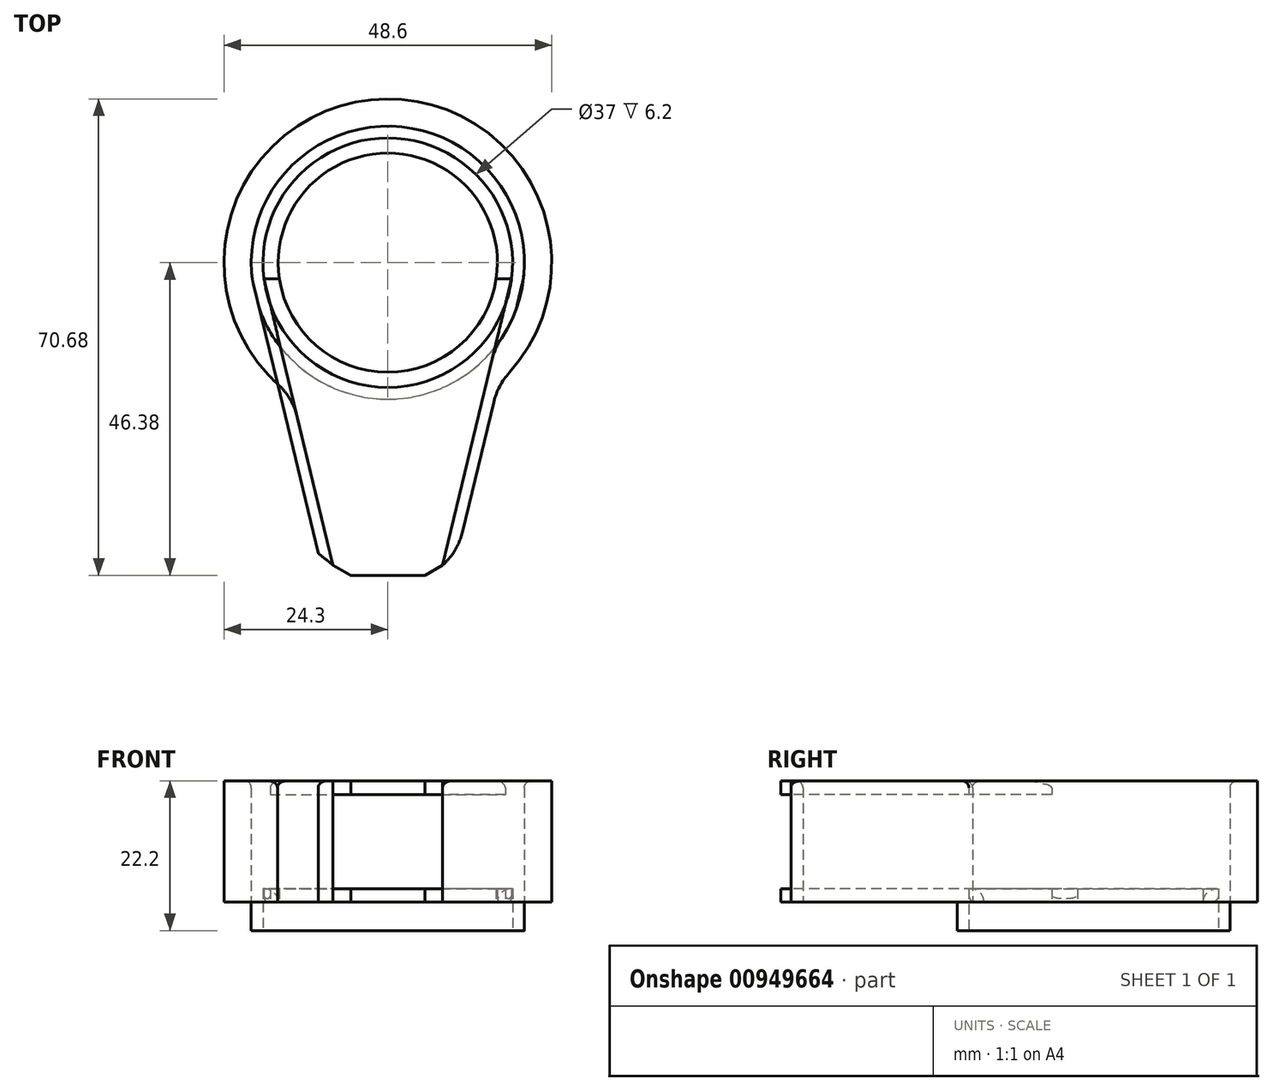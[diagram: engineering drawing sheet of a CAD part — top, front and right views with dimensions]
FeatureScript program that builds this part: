
annotation { "Feature Type Name" : "Feature", "Feature Type Description" : "" }
export const myFeature = defineFeature(function(context is Context, id is Id, definition is map)
    precondition{}
    {
        {
            var Q0;
            Q0=qCreatedBy(makeId("Top.planeOp"),FACE);
            var sketch = newSketch(context, id + "F0", { "sketchPlane" : qUnion([Q0])});
            skCircle(sketch, "E0", {"center": v(0, 0) * mm, "radius": 20.25 * mm});
            skCircle(sketch, "E1", {"center": v(0, 0) * mm, "radius": 24.3 * mm});
            skCircle(sketch, "E2", {"center": v(0, 0) * mm, "radius": 18.5 * mm});
            skArc(sketch, "E3", {"start": v(16.07, -2.4) * mm, "mid": v(0, 16.25) * mm, "end": v(-16.07, -2.4) * mm});
            skLineSegment(sketch, "E4", {"start": v(0, 0) * mm, "end": v(0, -46.38) * mm, "construction": true});
            skLineSegment(sketch, "E5", {"start": v(-16.07, -2.4) * mm, "end": v(-5.5, -46.38) * mm});
            skLineSegment(sketch, "E6", {"start": v(-5.5, -46.38) * mm, "end": v(0, -46.38) * mm});
            skLineSegment(sketch, "E7", {"start": v(-18.34, -2.4) * mm, "end": v(-8.13, -44.88) * mm});
            skLineSegment(sketch, "E8", {"start": v(-8.13, -44.88) * mm, "end": v(-5.5, -46.38) * mm});
            skLineSegment(sketch, "E9.MirrorCS", {"start": v(16.07, -2.4) * mm, "end": v(5.5, -46.38) * mm});
            skLineSegment(sketch, "E10.MirrorCS", {"start": v(18.34, -2.4) * mm, "end": v(8.13, -44.88) * mm});
            skLineSegment(sketch, "E11.MirrorCS", {"start": v(8.13, -44.88) * mm, "end": v(5.5, -46.38) * mm});
            skLineSegment(sketch, "E12.MirrorCS", {"start": v(5.5, -46.38) * mm, "end": v(0, -46.38) * mm});
            skLineSegment(sketch, "E13", {"start": v(-16.07, -2.4) * mm, "end": v(16.07, -2.4) * mm, "construction": true});
            skLineSegment(sketch, "E14", {"start": v(16.07, -2.4) * mm, "end": v(-16.07, -2.4) * mm});
            skLineSegment(sketch, "E15", {"start": v(-20.1, -2.4) * mm, "end": v(-10.32, -43.1) * mm});
            skLineSegment(sketch, "E16", {"start": v(-10.32, -43.1) * mm, "end": v(-8.13, -44.88) * mm});
            skLineSegment(sketch, "E17.MirrorCS", {"start": v(20.1, -2.4) * mm, "end": v(10.32, -43.1) * mm});
            skLineSegment(sketch, "E18.MirrorCS", {"start": v(10.32, -43.1) * mm, "end": v(8.13, -44.88) * mm});
            skCircle(sketch, "E19", {"center": v(0, 0) * mm, "radius": 16.25 * mm});
            skLineSegment(sketch, "E20", {"start": v(-16.07, -2.4) * mm, "end": v(-18.34, -2.4) * mm});
            skLineSegment(sketch, "E21", {"start": v(16.07, -2.4) * mm, "end": v(18.34, -2.4) * mm});
            skSolve(sketch);
        }
        {
            var Q0;
            {var subQ0=sQuery(id+"F0.wireOp",EDGE,"E3");Q0=makeQuery(id+"F0.imprint","IMPRINT",FACE,{"disambiguationData":[TD([[makeQuery(id+"F0.imprint","IMPRINT",EDGE,{"derivedFrom":subQ0}),-1.0]])]});}
            var Q1;
            {var subQ5=sQuery(id+"F0.wireOp",EDGE,"E8");Q1=makeQuery(id+"F0.imprint","IMPRINT",FACE,{"disambiguationData":[TD([[makeQuery(id+"F0.imprint","IMPRINT",EDGE,{"derivedFrom":subQ5}),1.0]])]});}
            var Q2;
            {var subQ5=sQuery(id+"F0.wireOp",EDGE,"E11.MirrorCS");Q2=makeQuery(id+"F0.imprint","IMPRINT",FACE,{"disambiguationData":[TD([[makeQuery(id+"F0.imprint","IMPRINT",EDGE,{"derivedFrom":subQ5}),-1.0]])]});}
            var Q3;
            {var subQ0=sQuery(id+"F0.wireOp",EDGE,"E9.MirrorCS");var subQ1=sQuery(id+"F0.wireOp",EDGE,"E0");var subQ2=makeQuery(id+"F0.imprint","INTERSECT",VERTEX,{"derivedFrom":[subQ1,subQ0]});Q3=makeQuery(id+"F0.imprint","IMPRINT",FACE,{"disambiguationData":[TD([[makeQuery(id+"F0.imprint","IMPRINT",EDGE,{"disambiguationData":[TD([[subQ2,-1.0]])],"derivedFrom":subQ1}),-1.0]])]});}
            var Q4;
            {var subQ0=sQuery(id+"F0.wireOp",EDGE,"E5");var subQ1=sQuery(id+"F0.wireOp",EDGE,"E0");var subQ2=makeQuery(id+"F0.imprint","INTERSECT",VERTEX,{"derivedFrom":[subQ1,subQ0]});Q4=makeQuery(id+"F0.imprint","IMPRINT",FACE,{"disambiguationData":[TD([[makeQuery(id+"F0.imprint","IMPRINT",EDGE,{"disambiguationData":[TD([[subQ2,1.0]])],"derivedFrom":subQ1}),-1.0]])]});}
            var Q5;
            {var subQ0=sQuery(id+"F0.wireOp",EDGE,"E9.MirrorCS");var subQ1=sQuery(id+"F0.wireOp",EDGE,"E0");var subQ2=makeQuery(id+"F0.imprint","INTERSECT",VERTEX,{"derivedFrom":[subQ1,subQ0]});Q5=makeQuery(id+"F0.imprint","IMPRINT",FACE,{"disambiguationData":[TD([[makeQuery(id+"F0.imprint","IMPRINT",EDGE,{"disambiguationData":[TD([[subQ2,-1.0]])],"derivedFrom":subQ1}),1.0]])]});}
            var Q6;
            {var subQ0=sQuery(id+"F0.wireOp",EDGE,"E5");var subQ1=sQuery(id+"F0.wireOp",EDGE,"E0");var subQ2=makeQuery(id+"F0.imprint","INTERSECT",VERTEX,{"derivedFrom":[subQ1,subQ0]});Q6=makeQuery(id+"F0.imprint","IMPRINT",FACE,{"disambiguationData":[TD([[makeQuery(id+"F0.imprint","IMPRINT",EDGE,{"disambiguationData":[TD([[subQ2,1.0]])],"derivedFrom":subQ1}),1.0]])]});}
            var Q7;
            {var subQ0=sQuery(id+"F0.wireOp",EDGE,"E6");Q7=makeQuery(id+"F0.imprint","IMPRINT",FACE,{"disambiguationData":[TD([[makeQuery(id+"F0.imprint","IMPRINT",EDGE,{"derivedFrom":subQ0}),1.0]])]});}
            var Q8;
            {var subQ0=sQuery(id+"F0.wireOp",EDGE,"E5");var subQ1=sQuery(id+"F0.wireOp",EDGE,"E0");var subQ2=makeQuery(id+"F0.imprint","INTERSECT",VERTEX,{"derivedFrom":[subQ1,subQ0]});Q8=makeQuery(id+"F0.imprint","IMPRINT",FACE,{"disambiguationData":[TD([[makeQuery(id+"F0.imprint","IMPRINT",EDGE,{"disambiguationData":[TD([[subQ2,-1.0]])],"derivedFrom":subQ1}),-1.0]])]});}
            var Q9;
            {var subQ0=sQuery(id+"F0.wireOp",EDGE,"E5");var subQ1=sQuery(id+"F0.wireOp",EDGE,"E0");var subQ2=makeQuery(id+"F0.imprint","INTERSECT",VERTEX,{"derivedFrom":[subQ1,subQ0]});Q9=makeQuery(id+"F0.imprint","IMPRINT",FACE,{"disambiguationData":[TD([[makeQuery(id+"F0.imprint","IMPRINT",EDGE,{"disambiguationData":[TD([[subQ2,-1.0]])],"derivedFrom":subQ1}),1.0]])]});}
            extrude(context, id + "F1", {"entities" : qUnion([Q0, Q1, Q2, Q3, Q4, Q5, Q6, Q7, Q8, Q9]), "depth" : 2 * mm, "offsetDistance" : 25 * mm});
        }
        {
            var Q0;
            {var subQ0=sQuery(id+"F0.wireOp",EDGE,"E7");var subQ1=sQuery(id+"F0.wireOp",EDGE,"E0");var subQ2=makeQuery(id+"F0.imprint","INTERSECT",VERTEX,{"derivedFrom":[subQ1,subQ0]});Q0=makeQuery(id+"F0.imprint","IMPRINT",FACE,{"disambiguationData":[TD([[makeQuery(id+"F0.imprint","IMPRINT",EDGE,{"disambiguationData":[TD([[subQ2,1.0]])],"derivedFrom":subQ1}),1.0]])]});}
            var Q1;
            {var subQ0=sQuery(id+"F0.wireOp",EDGE,"E5");var subQ1=sQuery(id+"F0.wireOp",EDGE,"E0");var subQ2=makeQuery(id+"F0.imprint","INTERSECT",VERTEX,{"derivedFrom":[subQ1,subQ0]});Q1=makeQuery(id+"F0.imprint","IMPRINT",FACE,{"disambiguationData":[TD([[makeQuery(id+"F0.imprint","IMPRINT",EDGE,{"disambiguationData":[TD([[subQ2,-1.0]])],"derivedFrom":subQ1}),1.0]])]});}
            var Q2;
            {var subQ0=sQuery(id+"F0.wireOp",EDGE,"E7");var subQ1=sQuery(id+"F0.wireOp",EDGE,"E0");var subQ2=makeQuery(id+"F0.imprint","INTERSECT",VERTEX,{"derivedFrom":[subQ1,subQ0]});Q2=makeQuery(id+"F0.imprint","IMPRINT",FACE,{"disambiguationData":[TD([[makeQuery(id+"F0.imprint","IMPRINT",EDGE,{"disambiguationData":[TD([[subQ2,-1.0]])],"derivedFrom":subQ1}),1.0]])]});}
            var Q3;
            {var subQ0=sQuery(id+"F0.wireOp",EDGE,"E9.MirrorCS");var subQ1=sQuery(id+"F0.wireOp",EDGE,"E0");var subQ2=makeQuery(id+"F0.imprint","INTERSECT",VERTEX,{"derivedFrom":[subQ1,subQ0]});Q3=makeQuery(id+"F0.imprint","IMPRINT",FACE,{"disambiguationData":[TD([[makeQuery(id+"F0.imprint","IMPRINT",EDGE,{"disambiguationData":[TD([[subQ2,-1.0]])],"derivedFrom":subQ1}),1.0]])]});}
            extrude(context, id + "F2", {"entities" : qUnion([Q0, Q1, Q2, Q3]), "operationType" : NewBodyOperationType.ADD, "oppositeDirection" : true, "depth" : 4.2 * mm, "offsetDistance" : 25 * mm});
        }
        {
            var Q0;
            {var subQ5=sQuery(id+"F0.wireOp",EDGE,"E16");Q0=makeQuery(id+"F0.imprint","IMPRINT",FACE,{"disambiguationData":[TD([[makeQuery(id+"F0.imprint","IMPRINT",EDGE,{"derivedFrom":subQ5}),1.0]])]});}
            var Q1;
            {var subQ0=sQuery(id+"F0.wireOp",EDGE,"E15");var subQ1=sQuery(id+"F0.wireOp",EDGE,"E0");var subQ2=makeQuery(id+"F0.imprint","INTERSECT",VERTEX,{"disambiguationData":[OD(1.0)],"derivedFrom":[subQ1,subQ0]});Q1=makeQuery(id+"F0.imprint","IMPRINT",FACE,{"disambiguationData":[TD([[makeQuery(id+"F0.imprint","IMPRINT",EDGE,{"disambiguationData":[TD([[subQ2,-1.0]])],"derivedFrom":subQ1}),-1.0]])]});}
            var Q2;
            {var subQ5=sQuery(id+"F0.wireOp",EDGE,"E0");var subQ8=sQuery(id+"F0.wireOp",EDGE,"E15");var subQ15=makeQuery(id+"F0.imprint","INTERSECT",VERTEX,{"disambiguationData":[OD(1.0)],"derivedFrom":[subQ5,subQ8]});Q2=makeQuery(id+"F0.imprint","IMPRINT",FACE,{"disambiguationData":[TD([[makeQuery(id+"F0.imprint","IMPRINT",EDGE,{"disambiguationData":[TD([[subQ15,-1.0]])],"derivedFrom":subQ5}),1.0]])]});}
            var Q3;
            {var subQ5=sQuery(id+"F0.wireOp",EDGE,"E18.MirrorCS");Q3=makeQuery(id+"F0.imprint","IMPRINT",FACE,{"disambiguationData":[TD([[makeQuery(id+"F0.imprint","IMPRINT",EDGE,{"derivedFrom":subQ5}),-1.0]])]});}
            var Q4;
            {var subQ0=sQuery(id+"F0.wireOp",EDGE,"E10.MirrorCS");var subQ1=sQuery(id+"F0.wireOp",EDGE,"E0");var subQ2=makeQuery(id+"F0.imprint","INTERSECT",VERTEX,{"derivedFrom":[subQ1,subQ0]});Q4=makeQuery(id+"F0.imprint","IMPRINT",FACE,{"disambiguationData":[TD([[makeQuery(id+"F0.imprint","IMPRINT",EDGE,{"disambiguationData":[TD([[subQ2,-1.0]])],"derivedFrom":subQ1}),-1.0]])]});}
            extrude(context, id + "F3", {"entities" : qUnion([Q0, Q1, Q2, Q3, Q4]), "depth" : 18 * mm, "offsetDistance" : 25 * mm});
        }
        {
            var Q0;
            {var subQ1=sQuery(id+"F0.wireOp",EDGE,"E2");var subQ8=sQuery(id+"F0.wireOp",EDGE,"E7");var subQ15=makeQuery(id+"F0.imprint","INTERSECT",VERTEX,{"disambiguationData":[OD(1.0)],"derivedFrom":[subQ1,subQ8]});Q0=makeQuery(id+"F0.imprint","IMPRINT",FACE,{"disambiguationData":[TD([[makeQuery(id+"F0.imprint","IMPRINT",EDGE,{"disambiguationData":[TD([[subQ15,-1.0]])],"derivedFrom":subQ1}),1.0]])]});}
            var Q1;
            {var subQ0=sQuery(id+"F0.wireOp",EDGE,"E5");var subQ1=sQuery(id+"F0.wireOp",EDGE,"E2");var subQ2=makeQuery(id+"F0.imprint","INTERSECT",VERTEX,{"derivedFrom":[subQ1,subQ0]});Q1=makeQuery(id+"F0.imprint","IMPRINT",FACE,{"disambiguationData":[TD([[makeQuery(id+"F0.imprint","IMPRINT",EDGE,{"disambiguationData":[TD([[subQ2,-1.0]])],"derivedFrom":subQ1}),1.0]])]});}
            var Q2;
            {var subQ0=sQuery(id+"F0.wireOp",EDGE,"E20");Q2=makeQuery(id+"F0.imprint","IMPRINT",FACE,{"disambiguationData":[TD([[makeQuery(id+"F0.imprint","IMPRINT",EDGE,{"derivedFrom":subQ0}),-1.0]])]});}
            var Q3;
            {var subQ0=sQuery(id+"F0.wireOp",EDGE,"E21");Q3=makeQuery(id+"F0.imprint","IMPRINT",FACE,{"disambiguationData":[TD([[makeQuery(id+"F0.imprint","IMPRINT",EDGE,{"derivedFrom":subQ0}),-1.0]])]});}
            extrude(context, id + "F4", {"entities" : qUnion([Q0, Q1, Q2, Q3]), "depth" : 2 * mm, "offsetDistance" : 25 * mm});
        }
        {
            var Q0;
            Q0=makeQuery(id+"F4.opExtrude","CAP_EDGE",EDGE,{"disambiguationData":[OSD([sQuery(id+"F0.wireOp",EDGE,"E19")])],"isStart":false});
            fillet(context, id + "F5", {"entities" : qUnion([Q0]), "radius" : 2 * mm, "tangentPropagation" : true, "allowEdgeOverflow" : false});
        }
        {
            var Q0;
            {var subQ0=sQuery(id+"F0.wireOp",EDGE,"E2");var subQ1=makeQuery(id+"F0.imprint","INTERSECT",VERTEX,{"derivedFrom":[subQ0,sQuery(id+"F0.wireOp",EDGE,"E9.MirrorCS")]});var subQ2=makeQuery(id+"F0.imprint","INTERSECT",VERTEX,{"derivedFrom":[subQ0,sQuery(id+"F0.wireOp",EDGE,"E5")]});Q0=makeQuery(id+"F4.opExtrude","CAP_EDGE",EDGE,{"disambiguationData":[OSD([subQ0]),TDD([makeQuery(id+"F0.imprint","IMPRINT",EDGE,{"disambiguationData":[TD([[makeQuery(id+"F0.imprint","INTERSECT",VERTEX,{"disambiguationData":[OD(1.0)],"derivedFrom":[subQ0,sQuery(id+"F0.wireOp",EDGE,"E7")]}),-1.0]])],"derivedFrom":subQ0}),makeQuery(id+"F0.imprint","IMPRINT",EDGE,{"disambiguationData":[TD([[subQ2,-1.0]])],"derivedFrom":subQ0}),makeQuery(id+"F0.imprint","IMPRINT",EDGE,{"disambiguationData":[TD([[subQ1,-1.0]])],"derivedFrom":subQ0})])],"isStart":true});}
            fillet(context, id + "F6", {"entities" : qUnion([Q0]), "radius" : 1 * mm, "tangentPropagation" : true, "allowEdgeOverflow" : false});
        }
        {
            var Q0;
            Q0=makeQuery(id+"F3.opExtrude","SWEPT_EDGE",EDGE,{"disambiguationData":[OSD([sQuery(id+"F0.wireOp",EDGE,"E2"),sQuery(id+"F0.wireOp",EDGE,"E7")])]});
            var Q1;
            Q1=makeQuery(id+"F3.opExtrude","SWEPT_EDGE",EDGE,{"disambiguationData":[OSD([sQuery(id+"F0.wireOp",EDGE,"E2"),sQuery(id+"F0.wireOp",EDGE,"E10.MirrorCS")])]});
            var Q2;
            Q2=makeQuery(id+"F3.opExtrude","SWEPT_EDGE",EDGE,{"disambiguationData":[OSD([sQuery(id+"F0.wireOp",EDGE,"E0"),sQuery(id+"F0.wireOp",EDGE,"E17.MirrorCS")])]});
            var Q3;
            {var subQ0=sQuery(id+"F0.wireOp",EDGE,"E17.MirrorCS");var subQ1=sQuery(id+"F0.wireOp",EDGE,"E0");Q3=makeQuery(id+"F2.opExtrude","SWEPT_EDGE",EDGE,{"disambiguationData":[OSD([subQ1,subQ0]),TDD([makeQuery(id+"F0.imprint","INTERSECT",VERTEX,{"disambiguationData":[OD(0.0)],"derivedFrom":[subQ1,subQ0]})])]});}
            var Q4;
            {var subQ0=sQuery(id+"F0.wireOp",EDGE,"E15");var subQ1=sQuery(id+"F0.wireOp",EDGE,"E0");Q4=makeQuery(id+"F2.opExtrude","SWEPT_EDGE",EDGE,{"disambiguationData":[OSD([subQ1,subQ0]),TDD([makeQuery(id+"F0.imprint","INTERSECT",VERTEX,{"disambiguationData":[OD(1.0)],"derivedFrom":[subQ1,subQ0]})])]});}
            var Q5;
            {var subQ0=sQuery(id+"F0.wireOp",EDGE,"E15");var subQ1=sQuery(id+"F0.wireOp",EDGE,"E0");Q5=makeQuery(id+"F2.opExtrude","SWEPT_EDGE",EDGE,{"disambiguationData":[OSD([subQ1,subQ0]),TDD([makeQuery(id+"F0.imprint","INTERSECT",VERTEX,{"disambiguationData":[OD(0.0)],"derivedFrom":[subQ1,subQ0]})])]});}
            var Q6;
            Q6=makeQuery(id+"F3.opExtrude","SWEPT_EDGE",EDGE,{"disambiguationData":[OSD([sQuery(id+"F0.wireOp",EDGE,"E0"),sQuery(id+"F0.wireOp",EDGE,"E15")])]});
            var Q7;
            {var subQ0=sQuery(id+"F0.wireOp",EDGE,"E17.MirrorCS");var subQ1=sQuery(id+"F0.wireOp",EDGE,"E0");Q7=makeQuery(id+"F2.opExtrude","SWEPT_EDGE",EDGE,{"disambiguationData":[OSD([subQ1,subQ0]),TDD([makeQuery(id+"F0.imprint","INTERSECT",VERTEX,{"disambiguationData":[OD(1.0)],"derivedFrom":[subQ1,subQ0]})])]});}
            fillet(context, id + "F7", {"entities" : qUnion([Q0, Q1, Q2, Q3, Q4, Q5, Q6, Q7]), "radius" : 10 * mm, "tangentPropagation" : true, "allowEdgeOverflow" : false});
        }
        {
            var Q0;
            Q0=makeQuery(id+"F1.opExtrude","CAP_FACE",FACE,{"disambiguationData":[OSD([sQuery(id+"F0.wireOp",EDGE,"E2"),sQuery(id+"F0.wireOp",EDGE,"E6"),sQuery(id+"F0.wireOp",EDGE,"E7"),sQuery(id+"F0.wireOp",EDGE,"E8"),sQuery(id+"F0.wireOp",EDGE,"E10.MirrorCS"),sQuery(id+"F0.wireOp",EDGE,"E11.MirrorCS"),sQuery(id+"F0.wireOp",EDGE,"E12.MirrorCS")])],"isStart":false});
            extrude(context, id + "F8", {"entities" : qUnion([Q0]), "depth" : 16 * mm, "offsetDistance" : 25 * mm});
        }
        {
            var Q0;
            Q0=makeQuery(id+"F1.opExtrude","CAP_FACE",FACE,{"disambiguationData":[OSD([sQuery(id+"F0.wireOp",EDGE,"E2"),sQuery(id+"F0.wireOp",EDGE,"E6"),sQuery(id+"F0.wireOp",EDGE,"E7"),sQuery(id+"F0.wireOp",EDGE,"E8"),sQuery(id+"F0.wireOp",EDGE,"E10.MirrorCS"),sQuery(id+"F0.wireOp",EDGE,"E11.MirrorCS"),sQuery(id+"F0.wireOp",EDGE,"E12.MirrorCS")])],"isStart":false});
            extrude(context, id + "F9", {"entities" : qUnion([Q0]), "operationType" : NewBodyOperationType.REMOVE, "depth" : 14 * mm, "offsetDistance" : 25 * mm});
        }
        {
            var Q0;
            Q0=makeQuery(id+"F3.opExtrude","CAP_EDGE",EDGE,{"disambiguationData":[OSD([sQuery(id+"F0.wireOp",EDGE,"E15")])],"isStart":false});
            fillet(context, id + "F10", {"entities" : qUnion([Q0]), "radius" : 1 * mm, "tangentPropagation" : true, "allowEdgeOverflow" : false});
        }
        {
            var Q0;
            Q0=makeQuery(id+"F3.opExtrude","CAP_EDGE",EDGE,{"disambiguationData":[OSD([sQuery(id+"F0.wireOp",EDGE,"E2")])],"isStart":false});
            var Q1;
            Q1=makeQuery(id+"F8.opExtrude","CAP_EDGE",EDGE,{"disambiguationData":[OSD([sQuery(id+"F0.wireOp",EDGE,"E2")])],"isStart":false});
            var Q2;
            Q2=makeQuery(id+"F9.boolean.opBoolean","COPY",EDGE,{"derivedFrom":makeQuery(id+"F9.opExtrude","CAP_EDGE",EDGE,{"disambiguationData":[OSD([sQuery(id+"F0.wireOp",EDGE,"E2")])],"isStart":false})});
            fillet(context, id + "F11", {"entities" : qUnion([Q0, Q1, Q2]), "radius" : 1 * mm, "allowEdgeOverflow" : false});
        }
    });
